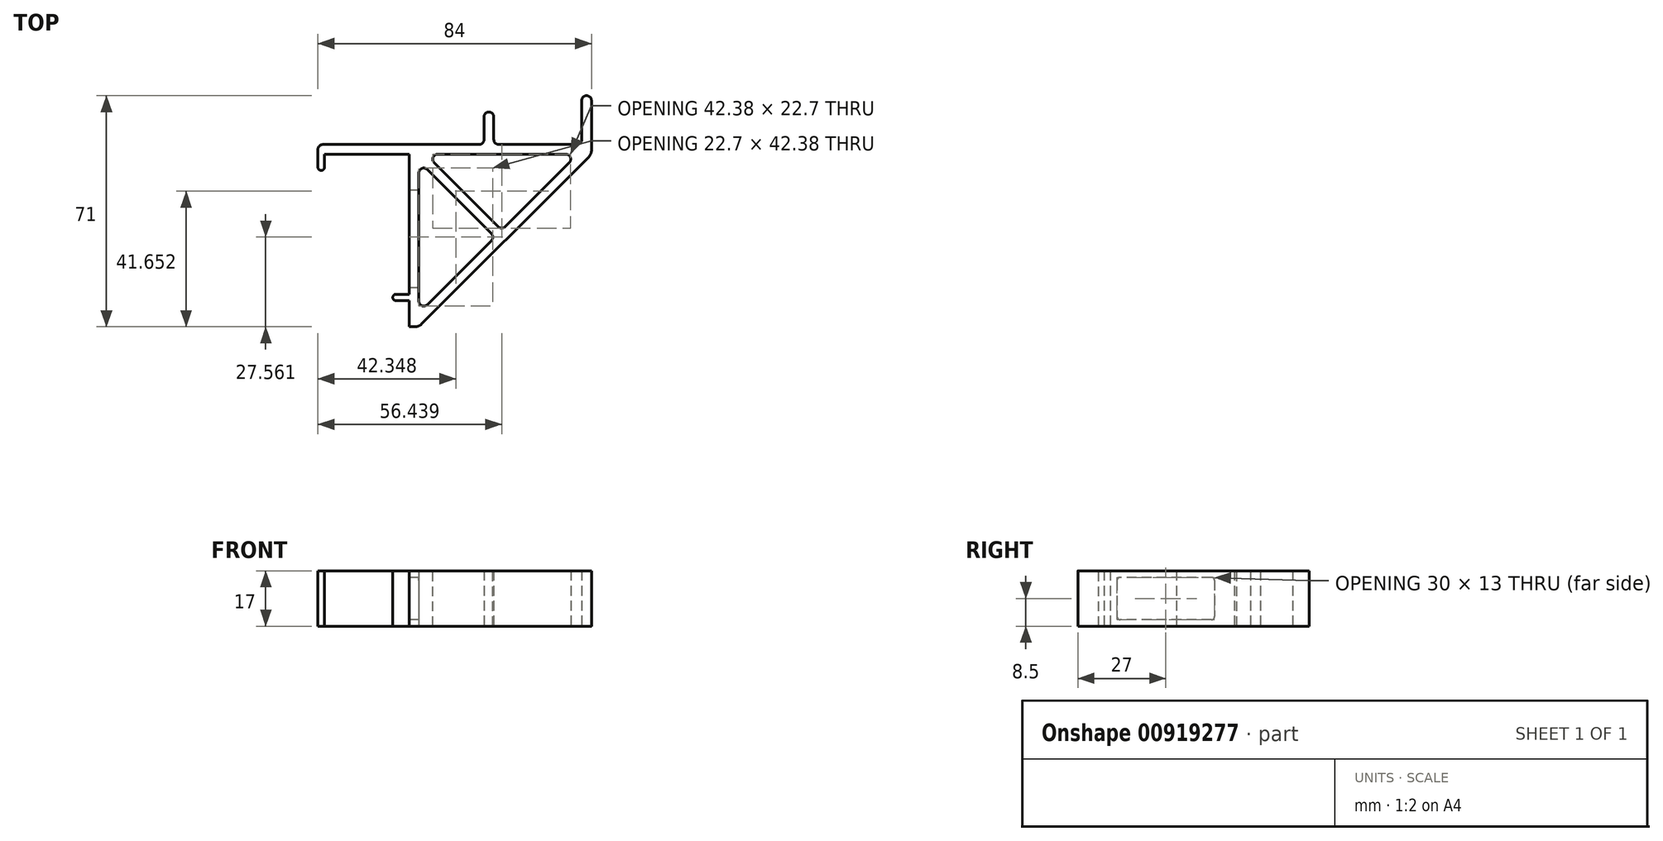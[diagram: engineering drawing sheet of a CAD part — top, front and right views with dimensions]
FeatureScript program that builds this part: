
annotation { "Feature Type Name" : "Feature", "Feature Type Description" : "" }
export const myFeature = defineFeature(function(context is Context, id is Id, definition is map)
    precondition{}
    {
        {
            var Q0;
            Q0=qCreatedBy(makeId("Top.planeOp"),FACE);
            var sketch = newSketch(context, id + "F0", { "sketchPlane" : qUnion([Q0])});
            skLineSegment(sketch, "E0.bottom", {"start": v(0, 0) * mm, "end": v(-3, 0) * mm});
            skLineSegment(sketch, "E0.top", {"start": v(0, 56) * mm, "end": v(-3, 56) * mm});
            skLineSegment(sketch, "E0.left", {"start": v(0, 0) * mm, "end": v(0, 56) * mm});
            skLineSegment(sketch, "E0.right", {"start": v(-3, 0) * mm, "end": v(-3, 56) * mm});
            skLineSegment(sketch, "E1.bottom", {"start": v(-3, 56) * mm, "end": v(-31, 56) * mm});
            skLineSegment(sketch, "E1.top", {"start": v(-3, 53) * mm, "end": v(-31, 53) * mm});
            skLineSegment(sketch, "E1.left", {"start": v(-3, 56) * mm, "end": v(-3, 53) * mm});
            skLineSegment(sketch, "E1.right", {"start": v(-31, 56) * mm, "end": v(-31, 53) * mm});
            skLineSegment(sketch, "E2.bottom", {"start": v(-31, 53) * mm, "end": v(-29, 53) * mm});
            skLineSegment(sketch, "E2.top", {"start": v(-31, 48) * mm, "end": v(-29, 48) * mm});
            skLineSegment(sketch, "E2.left", {"start": v(-31, 53) * mm, "end": v(-31, 48) * mm});
            skLineSegment(sketch, "E2.right", {"start": v(-29, 53) * mm, "end": v(-29, 48) * mm});
            skLineSegment(sketch, "E3", {"start": v(0, 56) * mm, "end": v(20, 56) * mm});
            skLineSegment(sketch, "E4", {"start": v(20, 56) * mm, "end": v(20, 53) * mm});
            skLineSegment(sketch, "E5", {"start": v(20, 53) * mm, "end": v(0, 53) * mm});
            skLineSegment(sketch, "E6", {"start": v(20, 56) * mm, "end": v(50, 56) * mm});
            skLineSegment(sketch, "E7", {"start": v(50, 56) * mm, "end": v(50, 71) * mm});
            skLineSegment(sketch, "E8", {"start": v(50, 71) * mm, "end": v(53, 71) * mm});
            skLineSegment(sketch, "E9", {"start": v(53, 71) * mm, "end": v(53, 53) * mm});
            skLineSegment(sketch, "E10", {"start": v(53, 53) * mm, "end": v(20, 53) * mm});
            skLineSegment(sketch, "E11.bottom", {"start": v(20, 56) * mm, "end": v(23, 56) * mm});
            skLineSegment(sketch, "E11.top", {"start": v(20, 66) * mm, "end": v(23, 66) * mm});
            skLineSegment(sketch, "E11.left", {"start": v(20, 56) * mm, "end": v(20, 66) * mm});
            skLineSegment(sketch, "E11.right", {"start": v(23, 56) * mm, "end": v(23, 66) * mm});
            skLineSegment(sketch, "E12", {"start": v(53, 53) * mm, "end": v(0, 0) * mm});
            skLineSegment(sketch, "E13", {"start": v(48.76, 53) * mm, "end": v(0, 4.24) * mm});
            skLineSegment(sketch, "E14", {"start": v(0, 53) * mm, "end": v(24.38, 28.62) * mm, "construction": true});
            skLineSegment(sketch, "E15", {"start": v(0, 50.88) * mm, "end": v(23.32, 27.56) * mm});
            skLineSegment(sketch, "E16", {"start": v(2.12, 53) * mm, "end": v(25.44, 29.68) * mm});
            skLineSegment(sketch, "E17.bottom", {"start": v(-3, 10) * mm, "end": v(-8, 10) * mm});
            skLineSegment(sketch, "E17.top", {"start": v(-3, 8) * mm, "end": v(-8, 8) * mm});
            skLineSegment(sketch, "E17.left", {"start": v(-3, 10) * mm, "end": v(-3, 8) * mm});
            skLineSegment(sketch, "E17.right", {"start": v(-8, 10) * mm, "end": v(-8, 8) * mm});
            skSolve(sketch);
        }
        {
            var Q0;
            Q0=makeQuery(id+"F0.imprint","IMPRINT",FACE,{"disambiguationData":[TD([[makeQuery(id+"F0.imprint","IMPRINT",EDGE,{"derivedFrom":sQuery(id+"F0.wireOp",EDGE,"E2.top")}),1.0]])]});
            var Q1;
            Q1=makeQuery(id+"F0.imprint","IMPRINT",FACE,{"disambiguationData":[TD([[makeQuery(id+"F0.imprint","IMPRINT",EDGE,{"derivedFrom":sQuery(id+"F0.wireOp",EDGE,"M4fOHIvX-XdU5-MNJU-iWRd-jkvcOCtF8kl4.bottom")}),-1.0]])]});
            var Q2;
            Q2=makeQuery(id+"F0.imprint","IMPRINT",FACE,{"disambiguationData":[TD([[makeQuery(id+"F0.imprint","IMPRINT",EDGE,{"derivedFrom":sQuery(id+"F0.wireOp",EDGE,"E11.top")}),-1.0]])]});
            var Q3;
            {var subQ0=sQuery(id+"F0.wireOp",EDGE,"E17.bottom");Q3=makeQuery(id+"F0.imprint","IMPRINT",FACE,{"disambiguationData":[TD([[makeQuery(id+"F0.imprint","IMPRINT",EDGE,{"derivedFrom":subQ0}),1.0]])]});}
            var Q4;
            {var subQ5=sQuery(id+"F0.wireOp",EDGE,"E1.bottom");Q4=makeQuery(id+"F0.imprint","IMPRINT",FACE,{"disambiguationData":[TD([[makeQuery(id+"F0.imprint","IMPRINT",EDGE,{"derivedFrom":subQ5}),1.0]])]});}
            var Q5;
            {var subQ1=sQuery(id+"F0.wireOp",EDGE,"E3");Q5=makeQuery(id+"F0.imprint","IMPRINT",FACE,{"disambiguationData":[TD([[makeQuery(id+"F0.imprint","IMPRINT",EDGE,{"derivedFrom":subQ1}),-1.0]])]});}
            var Q6;
            {var subQ1=sQuery(id+"F0.wireOp",EDGE,"E4");Q6=makeQuery(id+"F0.imprint","IMPRINT",FACE,{"disambiguationData":[TD([[makeQuery(id+"F0.imprint","IMPRINT",EDGE,{"derivedFrom":subQ1}),1.0]])]});}
            var Q7;
            {var subQ0=sQuery(id+"F0.wireOp",EDGE,"E12");Q7=makeQuery(id+"F0.imprint","IMPRINT",FACE,{"disambiguationData":[TD([[makeQuery(id+"F0.imprint","IMPRINT",EDGE,{"derivedFrom":subQ0}),-1.0]])]});}
            var Q8;
            {var subQ1=sQuery(id+"F0.wireOp",EDGE,"E0.bottom");Q8=makeQuery(id+"F0.imprint","IMPRINT",FACE,{"disambiguationData":[TD([[makeQuery(id+"F0.imprint","IMPRINT",EDGE,{"derivedFrom":subQ1}),-1.0]])]});}
            var Q9;
            {var subQ0=sQuery(id+"F0.wireOp",EDGE,"E15");Q9=makeQuery(id+"F0.imprint","IMPRINT",FACE,{"disambiguationData":[TD([[makeQuery(id+"F0.imprint","IMPRINT",EDGE,{"derivedFrom":subQ0}),1.0]])]});}
            extrude(context, id + "F1", {"entities" : qUnion([Q0, Q1, Q2, Q3, Q4, Q5, Q6, Q7, Q8, Q9]), "depth" : 17 * mm, "offsetDistance" : 25 * mm});
        }
        {
            var Q0;
            Q0=makeQuery(id+"F1.opExtrude","SWEPT_EDGE",EDGE,{"disambiguationData":[OSD([sQuery(id+"F0.wireOp",EDGE,"E11.top"),sQuery(id+"F0.wireOp",EDGE,"E11.left")])]});
            var Q1;
            Q1=makeQuery(id+"F1.opExtrude","SWEPT_EDGE",EDGE,{"disambiguationData":[OSD([sQuery(id+"F0.wireOp",EDGE,"E11.top"),sQuery(id+"F0.wireOp",EDGE,"E11.right")])]});
            var Q2;
            Q2=makeQuery(id+"F1.opExtrude","SWEPT_EDGE",EDGE,{"disambiguationData":[OSD([sQuery(id+"F0.wireOp",EDGE,"E7"),sQuery(id+"F0.wireOp",EDGE,"E8")])]});
            var Q3;
            Q3=makeQuery(id+"F1.opExtrude","SWEPT_EDGE",EDGE,{"disambiguationData":[OSD([sQuery(id+"F0.wireOp",EDGE,"E8"),sQuery(id+"F0.wireOp",EDGE,"E9")])]});
            fillet(context, id + "F2", {"entities" : qUnion([Q0, Q1, Q2, Q3]), "radius" : 1.5 * mm, "tangentPropagation" : true, "allowEdgeOverflow" : false});
        }
        {
            var Q0;
            Q0=makeQuery(id+"F1.opExtrude","SWEPT_EDGE",EDGE,{"disambiguationData":[OSD([sQuery(id+"F0.wireOp",EDGE,"E9"),sQuery(id+"F0.wireOp",EDGE,"E10"),sQuery(id+"F0.wireOp",EDGE,"E12")])]});
            var Q1;
            Q1=makeQuery(id+"F1.opExtrude","SWEPT_EDGE",EDGE,{"disambiguationData":[OSD([sQuery(id+"F0.wireOp",EDGE,"E0.bottom"),sQuery(id+"F0.wireOp",EDGE,"E0.left"),sQuery(id+"F0.wireOp",EDGE,"E12")])]});
            fillet(context, id + "F3", {"entities" : qUnion([Q0, Q1]), "radius" : 3 * mm, "tangentPropagation" : true, "allowEdgeOverflow" : false});
        }
        {
            var Q0;
            Q0=makeQuery(id+"F1.opExtrude","SWEPT_EDGE",EDGE,{"disambiguationData":[OSD([sQuery(id+"F0.wireOp",EDGE,"E6"),sQuery(id+"F0.wireOp",EDGE,"E11.right")])]});
            var Q1;
            Q1=makeQuery(id+"F1.opExtrude","SWEPT_EDGE",EDGE,{"disambiguationData":[OSD([sQuery(id+"F0.wireOp",EDGE,"E6"),sQuery(id+"F0.wireOp",EDGE,"E7")])]});
            var Q2;
            Q2=makeQuery(id+"F1.opExtrude","SWEPT_EDGE",EDGE,{"disambiguationData":[OSD([sQuery(id+"F0.wireOp",EDGE,"E3"),sQuery(id+"F0.wireOp",EDGE,"E4"),sQuery(id+"F0.wireOp",EDGE,"E6"),sQuery(id+"F0.wireOp",EDGE,"E11.left")])]});
            var Q3;
            Q3=makeQuery(id+"F1.opExtrude","SWEPT_EDGE",EDGE,{"disambiguationData":[OSD([sQuery(id+"F0.wireOp",EDGE,"E1.bottom"),sQuery(id+"F0.wireOp",EDGE,"E1.right")])]});
            var Q4;
            Q4=makeQuery(id+"F1.opExtrude","SWEPT_EDGE",EDGE,{"disambiguationData":[OSD([sQuery(id+"F0.wireOp",EDGE,"tzTazZ0h-Mju9-QxRi-W33k-W2sHQxdAFYEA.top"),sQuery(id+"F0.wireOp",EDGE,"tzTazZ0h-Mju9-QxRi-W33k-W2sHQxdAFYEA.right")])]});
            var Q5;
            Q5=makeQuery(id+"F1.opExtrude","SWEPT_EDGE",EDGE,{"disambiguationData":[OSD([sQuery(id+"F0.wireOp",EDGE,"tzTazZ0h-Mju9-QxRi-W33k-W2sHQxdAFYEA.bottom"),sQuery(id+"F0.wireOp",EDGE,"tzTazZ0h-Mju9-QxRi-W33k-W2sHQxdAFYEA.right")])]});
            var Q6;
            Q6=makeQuery(id+"F1.opExtrude","SWEPT_EDGE",EDGE,{"disambiguationData":[OSD([sQuery(id+"F0.wireOp",EDGE,"E0.left"),sQuery(id+"F0.wireOp",EDGE,"E15")])]});
            var Q7;
            Q7=makeQuery(id+"F1.opExtrude","SWEPT_EDGE",EDGE,{"disambiguationData":[OSD([sQuery(id+"F0.wireOp",EDGE,"E5"),sQuery(id+"F0.wireOp",EDGE,"E16")])]});
            var Q8;
            Q8=makeQuery(id+"F1.opExtrude","SWEPT_EDGE",EDGE,{"disambiguationData":[OSD([sQuery(id+"F0.wireOp",EDGE,"E13"),sQuery(id+"F0.wireOp",EDGE,"E16")])]});
            var Q9;
            Q9=makeQuery(id+"F1.opExtrude","SWEPT_EDGE",EDGE,{"disambiguationData":[OSD([sQuery(id+"F0.wireOp",EDGE,"E0.left"),sQuery(id+"F0.wireOp",EDGE,"E13")])]});
            var Q10;
            Q10=makeQuery(id+"F1.opExtrude","SWEPT_EDGE",EDGE,{"disambiguationData":[OSD([sQuery(id+"F0.wireOp",EDGE,"E13"),sQuery(id+"F0.wireOp",EDGE,"E15")])]});
            var Q11;
            Q11=makeQuery(id+"F1.opExtrude","SWEPT_EDGE",EDGE,{"disambiguationData":[OSD([sQuery(id+"F0.wireOp",EDGE,"E10"),sQuery(id+"F0.wireOp",EDGE,"E13")])]});
            fillet(context, id + "F4", {"entities" : qUnion([Q0, Q1, Q2, Q3, Q4, Q5, Q6, Q7, Q8, Q9, Q10, Q11]), "radius" : 1.5 * mm, "tangentPropagation" : true, "allowEdgeOverflow" : false});
        }
        {
            var Q0;
            Q0=makeQuery(id+"F1.opExtrude","SWEPT_EDGE",EDGE,{"disambiguationData":[OSD([sQuery(id+"F0.wireOp",EDGE,"E2.top"),sQuery(id+"F0.wireOp",EDGE,"E2.left")])]});
            var Q1;
            Q1=makeQuery(id+"F1.opExtrude","SWEPT_EDGE",EDGE,{"disambiguationData":[OSD([sQuery(id+"F0.wireOp",EDGE,"E2.top"),sQuery(id+"F0.wireOp",EDGE,"E2.right")])]});
            var Q2;
            Q2=makeQuery(id+"F1.opExtrude","SWEPT_EDGE",EDGE,{"disambiguationData":[OSD([sQuery(id+"F0.wireOp",EDGE,"M4fOHIvX-XdU5-MNJU-iWRd-jkvcOCtF8kl4.top"),sQuery(id+"F0.wireOp",EDGE,"M4fOHIvX-XdU5-MNJU-iWRd-jkvcOCtF8kl4.left")])]});
            var Q3;
            Q3=makeQuery(id+"F1.opExtrude","SWEPT_EDGE",EDGE,{"disambiguationData":[OSD([sQuery(id+"F0.wireOp",EDGE,"M4fOHIvX-XdU5-MNJU-iWRd-jkvcOCtF8kl4.top"),sQuery(id+"F0.wireOp",EDGE,"M4fOHIvX-XdU5-MNJU-iWRd-jkvcOCtF8kl4.right")])]});
            var Q4;
            Q4=makeQuery(id+"F1.opExtrude","SWEPT_EDGE",EDGE,{"disambiguationData":[OSD([sQuery(id+"F0.wireOp",EDGE,"E17.bottom"),sQuery(id+"F0.wireOp",EDGE,"E17.right")])]});
            var Q5;
            Q5=makeQuery(id+"F1.opExtrude","SWEPT_EDGE",EDGE,{"disambiguationData":[OSD([sQuery(id+"F0.wireOp",EDGE,"E17.top"),sQuery(id+"F0.wireOp",EDGE,"E17.right")])]});
            fillet(context, id + "F5", {"entities" : qUnion([Q0, Q1, Q2, Q3, Q4, Q5]), "radius" : 1 * mm, "tangentPropagation" : true, "allowEdgeOverflow" : false});
        }
        {
            var Q0;
            {var subQ0=sQuery(id+"F0.wireOp",EDGE,"E0.right");Q0=qUnion([makeQuery(id+"F1.opExtrude","SWEPT_FACE",FACE,{"disambiguationData":[OSD([subQ0]),TDD([makeQuery(id+"F0.imprint","IMPRINT",EDGE,{"disambiguationData":[TD([[makeQuery(id+"F0.imprint","INTERSECT",VERTEX,{"derivedFrom":[sQuery(id+"F0.wireOp",EDGE,"E0.bottom"),subQ0]}),-1.0]])],"derivedFrom":subQ0})])]}),makeQuery(id+"F1.opExtrude","SWEPT_FACE",FACE,{"disambiguationData":[OSD([subQ0]),TDD([makeQuery(id+"F0.imprint","IMPRINT",EDGE,{"disambiguationData":[TD([[makeQuery(id+"F0.imprint","INTERSECT",VERTEX,{"derivedFrom":[subQ0,sQuery(id+"F0.wireOp",EDGE,"E17.bottom")]}),-1.0]])],"derivedFrom":subQ0})])]})]);}
            var sketch = newSketch(context, id + "F6", { "sketchPlane" : qUnion([Q0])});
            skLineSegment(sketch, "E18.bottom", {"start": v(-12, 2) * mm, "end": v(-42, 2) * mm});
            skLineSegment(sketch, "E18.top", {"start": v(-12, 15) * mm, "end": v(-42, 15) * mm});
            skLineSegment(sketch, "E18.left", {"start": v(-12, 2) * mm, "end": v(-12, 15) * mm});
            skLineSegment(sketch, "E18.right", {"start": v(-42, 2) * mm, "end": v(-42, 15) * mm});
            skSolve(sketch);
        }
        {
            var Q0;
            Q0 = qSketchRegion(id + "F6", true);
            var Q1;
            Q1=makeQuery(id+"F1.opExtrude","SWEPT_FACE",FACE,{"disambiguationData":[OSD([sQuery(id+"F0.wireOp",EDGE,"E0.left")])]});
            extrude(context, id + "F7", {"entities" : qUnion([Q0]), "operationType" : NewBodyOperationType.REMOVE, "endBound" : BoundingType.UP_TO_SURFACE, "oppositeDirection" : true, "depth" : 25 * mm, "endBoundEntityFace" : qUnion([Q1]), "offsetDistance" : 25 * mm});
        }
        {
            var Q0;
            Q0=makeQuery(id+"F7.boolean.opBoolean","COPY",EDGE,{"derivedFrom":makeQuery(id+"F7.opExtrude","SWEPT_EDGE",EDGE,{"disambiguationData":[OSD([sQuery(id+"F6.wireOp",EDGE,"E18.bottom"),sQuery(id+"F6.wireOp",EDGE,"E18.left")])]})});
            var Q1;
            Q1=makeQuery(id+"FxSZJegbLzRS3bu_1.boolean.opBoolean","COPY",EDGE,{"derivedFrom":makeQuery(id+"FxSZJegbLzRS3bu_1.opExtrude","SWEPT_EDGE",EDGE,{"disambiguationData":[OSD([sQuery(id+"FVKKvuaJUfCOsZX_1.wireOp",EDGE,"r5pYmvoD-I60V-4obB-Ckvy-1b26ltSggzgB.bottom"),sQuery(id+"FVKKvuaJUfCOsZX_1.wireOp",EDGE,"r5pYmvoD-I60V-4obB-Ckvy-1b26ltSggzgB.right")])]})});
            var Q2;
            Q2=makeQuery(id+"FxSZJegbLzRS3bu_1.boolean.opBoolean","COPY",EDGE,{"derivedFrom":makeQuery(id+"FxSZJegbLzRS3bu_1.opExtrude","SWEPT_EDGE",EDGE,{"disambiguationData":[OSD([sQuery(id+"FVKKvuaJUfCOsZX_1.wireOp",EDGE,"CLJGBW9T-tpro-oQ8P-e1xi-DiNSBggARnuw.bottom"),sQuery(id+"FVKKvuaJUfCOsZX_1.wireOp",EDGE,"CLJGBW9T-tpro-oQ8P-e1xi-DiNSBggARnuw.right")])]})});
            var Q3;
            Q3=makeQuery(id+"FxSZJegbLzRS3bu_1.boolean.opBoolean","COPY",EDGE,{"derivedFrom":makeQuery(id+"FxSZJegbLzRS3bu_1.opExtrude","SWEPT_EDGE",EDGE,{"disambiguationData":[OSD([sQuery(id+"FVKKvuaJUfCOsZX_1.wireOp",EDGE,"r5pYmvoD-I60V-4obB-Ckvy-1b26ltSggzgB.bottom"),sQuery(id+"FVKKvuaJUfCOsZX_1.wireOp",EDGE,"r5pYmvoD-I60V-4obB-Ckvy-1b26ltSggzgB.left")])]})});
            var Q4;
            Q4=makeQuery(id+"FxSZJegbLzRS3bu_1.boolean.opBoolean","COPY",EDGE,{"derivedFrom":makeQuery(id+"FxSZJegbLzRS3bu_1.opExtrude","SWEPT_EDGE",EDGE,{"disambiguationData":[OSD([sQuery(id+"FVKKvuaJUfCOsZX_1.wireOp",EDGE,"CLJGBW9T-tpro-oQ8P-e1xi-DiNSBggARnuw.bottom"),sQuery(id+"FVKKvuaJUfCOsZX_1.wireOp",EDGE,"CLJGBW9T-tpro-oQ8P-e1xi-DiNSBggARnuw.left")])]})});
            var Q5;
            Q5=makeQuery(id+"FxSZJegbLzRS3bu_1.boolean.opBoolean","COPY",EDGE,{"derivedFrom":makeQuery(id+"FxSZJegbLzRS3bu_1.opExtrude","SWEPT_EDGE",EDGE,{"disambiguationData":[OSD([sQuery(id+"FVKKvuaJUfCOsZX_1.wireOp",EDGE,"CLJGBW9T-tpro-oQ8P-e1xi-DiNSBggARnuw.top"),sQuery(id+"FVKKvuaJUfCOsZX_1.wireOp",EDGE,"CLJGBW9T-tpro-oQ8P-e1xi-DiNSBggARnuw.right")])]})});
            var Q6;
            Q6=makeQuery(id+"FxSZJegbLzRS3bu_1.boolean.opBoolean","COPY",EDGE,{"derivedFrom":makeQuery(id+"FxSZJegbLzRS3bu_1.opExtrude","SWEPT_EDGE",EDGE,{"disambiguationData":[OSD([sQuery(id+"FVKKvuaJUfCOsZX_1.wireOp",EDGE,"r5pYmvoD-I60V-4obB-Ckvy-1b26ltSggzgB.top"),sQuery(id+"FVKKvuaJUfCOsZX_1.wireOp",EDGE,"r5pYmvoD-I60V-4obB-Ckvy-1b26ltSggzgB.right")])]})});
            var Q7;
            Q7=makeQuery(id+"FxSZJegbLzRS3bu_1.boolean.opBoolean","COPY",EDGE,{"derivedFrom":makeQuery(id+"FxSZJegbLzRS3bu_1.opExtrude","SWEPT_EDGE",EDGE,{"disambiguationData":[OSD([sQuery(id+"FVKKvuaJUfCOsZX_1.wireOp",EDGE,"r5pYmvoD-I60V-4obB-Ckvy-1b26ltSggzgB.top"),sQuery(id+"FVKKvuaJUfCOsZX_1.wireOp",EDGE,"r5pYmvoD-I60V-4obB-Ckvy-1b26ltSggzgB.left")])]})});
            var Q8;
            Q8=makeQuery(id+"FxSZJegbLzRS3bu_1.boolean.opBoolean","COPY",EDGE,{"derivedFrom":makeQuery(id+"FxSZJegbLzRS3bu_1.opExtrude","SWEPT_EDGE",EDGE,{"disambiguationData":[OSD([sQuery(id+"FVKKvuaJUfCOsZX_1.wireOp",EDGE,"CLJGBW9T-tpro-oQ8P-e1xi-DiNSBggARnuw.top"),sQuery(id+"FVKKvuaJUfCOsZX_1.wireOp",EDGE,"CLJGBW9T-tpro-oQ8P-e1xi-DiNSBggARnuw.left")])]})});
            var Q9;
            Q9=makeQuery(id+"F7.boolean.opBoolean","COPY",EDGE,{"derivedFrom":makeQuery(id+"F7.opExtrude","SWEPT_EDGE",EDGE,{"disambiguationData":[OSD([sQuery(id+"F6.wireOp",EDGE,"E18.bottom"),sQuery(id+"F6.wireOp",EDGE,"E18.right")])]})});
            var Q10;
            Q10=makeQuery(id+"F7.boolean.opBoolean","COPY",EDGE,{"derivedFrom":makeQuery(id+"F7.opExtrude","SWEPT_EDGE",EDGE,{"disambiguationData":[OSD([sQuery(id+"F6.wireOp",EDGE,"E18.top"),sQuery(id+"F6.wireOp",EDGE,"E18.right")])]})});
            var Q11;
            Q11=makeQuery(id+"F7.boolean.opBoolean","COPY",EDGE,{"derivedFrom":makeQuery(id+"F7.opExtrude","SWEPT_EDGE",EDGE,{"disambiguationData":[OSD([sQuery(id+"F6.wireOp",EDGE,"E18.top"),sQuery(id+"F6.wireOp",EDGE,"E18.left")])]})});
            fillet(context, id + "F8", {"entities" : qUnion([Q0, Q1, Q2, Q3, Q4, Q5, Q6, Q7, Q8, Q9, Q10, Q11]), "radius" : 1 * mm, "tangentPropagation" : true, "allowEdgeOverflow" : false});
        }
    });
